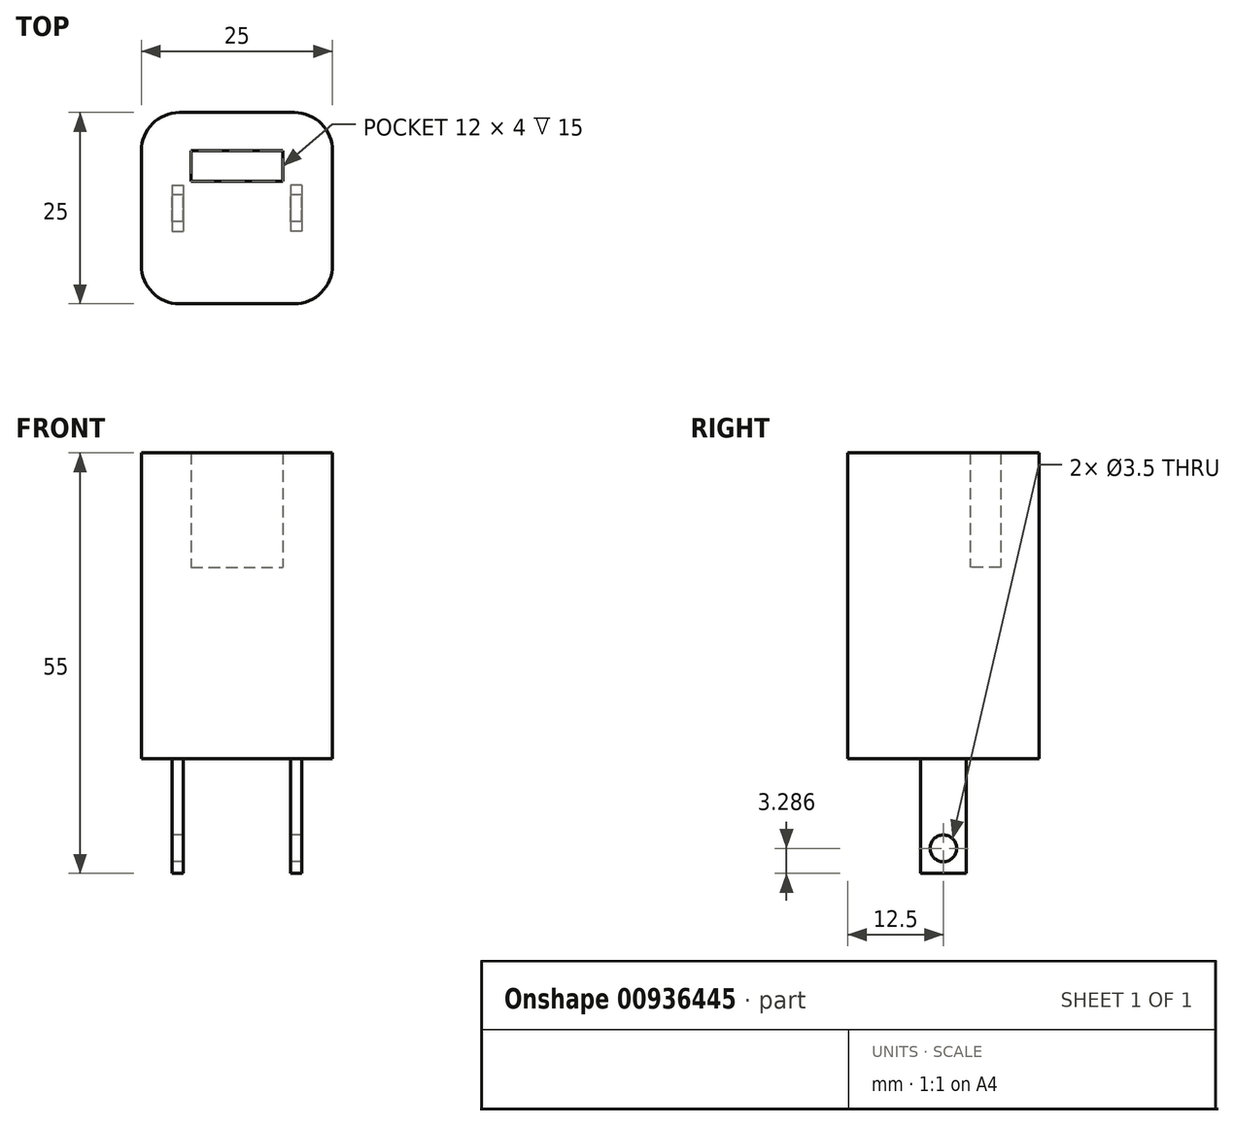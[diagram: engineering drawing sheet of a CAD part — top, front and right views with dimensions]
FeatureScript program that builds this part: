
annotation { "Feature Type Name" : "Feature", "Feature Type Description" : "" }
export const myFeature = defineFeature(function(context is Context, id is Id, definition is map)
    precondition{}
    {
        {
            var Q0;
            Q0=qCreatedBy(makeId("Top.planeOp"),FACE);
            var sketch = newSketch(context, id + "F0", { "sketchPlane" : qUnion([Q0])});
            skLineSegment(sketch, "E0.bottom", {"start": v(12.5, 12.5) * mm, "end": v(-12.5, 12.5) * mm});
            skLineSegment(sketch, "E0.top", {"start": v(12.5, -12.5) * mm, "end": v(-12.5, -12.5) * mm});
            skLineSegment(sketch, "E0.left", {"start": v(12.5, 12.5) * mm, "end": v(12.5, -12.5) * mm});
            skLineSegment(sketch, "E0.right", {"start": v(-12.5, 12.5) * mm, "end": v(-12.5, -12.5) * mm});
            skPoint(sketch, "E0.middle", {"position": v(0, 0) * mm});
            skLineSegment(sketch, "E1.bottom", {"start": v(-6, 7.5) * mm, "end": v(6, 7.5) * mm});
            skLineSegment(sketch, "E1.top", {"start": v(-6, 3.5) * mm, "end": v(6, 3.5) * mm});
            skLineSegment(sketch, "E1.left", {"start": v(-6, 7.5) * mm, "end": v(-6, 3.5) * mm});
            skLineSegment(sketch, "E1.right", {"start": v(6, 7.5) * mm, "end": v(6, 3.5) * mm});
            skSolve(sketch);
        }
        {
            var Q0;
            Q0=makeQuery(id+"F0.imprint","IMPRINT",FACE,{"disambiguationData":[TD([[makeQuery(id+"F0.imprint","IMPRINT",EDGE,{"derivedFrom":sQuery(id+"F0.wireOp",EDGE,"E0.bottom")}),1.0]])]});
            extrude(context, id + "F1", {"entities" : qUnion([Q0]), "depth" : 40 * mm, "offsetDistance" : 25 * mm});
        }
        {
            var Q0;
            Q0=makeQuery(id+"F1.opExtrude","CAP_FACE",FACE,{"disambiguationData":[OSD([sQuery(id+"F0.wireOp",EDGE,"E0.bottom"),sQuery(id+"F0.wireOp",EDGE,"E0.top"),sQuery(id+"F0.wireOp",EDGE,"E0.left"),sQuery(id+"F0.wireOp",EDGE,"E0.right"),sQuery(id+"F0.wireOp",EDGE,"E1.bottom"),sQuery(id+"F0.wireOp",EDGE,"E1.top"),sQuery(id+"F0.wireOp",EDGE,"E1.left"),sQuery(id+"F0.wireOp",EDGE,"E1.right")])],"isStart":true});
            var sketch = newSketch(context, id + "F2", { "sketchPlane" : qUnion([Q0])});
            skLineSegment(sketch, "E2.bottom", {"start": v(-8.5, -3) * mm, "end": v(-7, -3) * mm});
            skLineSegment(sketch, "E2.top", {"start": v(-8.5, 3) * mm, "end": v(-7, 3) * mm});
            skLineSegment(sketch, "E2.left", {"start": v(-8.5, -3) * mm, "end": v(-8.5, 3) * mm});
            skLineSegment(sketch, "E2.right", {"start": v(-7, -3) * mm, "end": v(-7, 3) * mm});
            skLineSegment(sketch, "E3.bottom", {"start": v(8.5, -3) * mm, "end": v(7, -3) * mm});
            skLineSegment(sketch, "E3.top", {"start": v(8.5, 3) * mm, "end": v(7, 3) * mm});
            skLineSegment(sketch, "E3.left", {"start": v(8.5, -3) * mm, "end": v(8.5, 3) * mm});
            skLineSegment(sketch, "E3.right", {"start": v(7, -3) * mm, "end": v(7, 3) * mm});
            skSolve(sketch);
        }
        {
            var Q0;
            Q0 = qSketchRegion(id + "F2", true);
            extrude(context, id + "F3", {"entities" : qUnion([Q0]), "operationType" : NewBodyOperationType.ADD, "depth" : 15 * mm, "offsetDistance" : 25 * mm});
        }
        {
            var Q0;
            Q0=makeQuery(id+"F3.opExtrude","SWEPT_FACE",FACE,{"disambiguationData":[OSD([sQuery(id+"F2.wireOp",EDGE,"E2.left")])]});
            var sketch = newSketch(context, id + "F4", { "sketchPlane" : qUnion([Q0])});
            skCircle(sketch, "E4", {"center": v(0, -11.71) * mm, "radius": 1.75 * mm});
            skSolve(sketch);
        }
        {
            var Q0;
            Q0 = qSketchRegion(id + "F4", true);
            extrude(context, id + "F5", {"entities" : qUnion([Q0]), "operationType" : NewBodyOperationType.REMOVE, "oppositeDirection" : true, "depth" : 25 * mm, "offsetDistance" : 25 * mm});
        }
        {
            var Q0;
            Q0=makeQuery(id+"F1.opExtrude","CAP_FACE",FACE,{"disambiguationData":[OSD([sQuery(id+"F0.wireOp",EDGE,"E0.bottom"),sQuery(id+"F0.wireOp",EDGE,"E0.top"),sQuery(id+"F0.wireOp",EDGE,"E0.left"),sQuery(id+"F0.wireOp",EDGE,"E0.right"),sQuery(id+"F0.wireOp",EDGE,"E1.bottom"),sQuery(id+"F0.wireOp",EDGE,"E1.top"),sQuery(id+"F0.wireOp",EDGE,"E1.left"),sQuery(id+"F0.wireOp",EDGE,"E1.right")])],"isStart":true});
            var sketch = newSketch(context, id + "F6", { "sketchPlane" : qUnion([Q0])});
            skLineSegment(sketch, "E5.bottom", {"start": v(6, -7.5) * mm, "end": v(-6, -7.5) * mm});
            skLineSegment(sketch, "E5.top", {"start": v(6, -3.5) * mm, "end": v(-6, -3.5) * mm});
            skLineSegment(sketch, "E5.left", {"start": v(6, -7.5) * mm, "end": v(6, -3.5) * mm});
            skLineSegment(sketch, "E5.right", {"start": v(-6, -7.5) * mm, "end": v(-6, -3.5) * mm});
            skSolve(sketch);
        }
        {
            var Q0;
            Q0 = qSketchRegion(id + "F6", true);
            extrude(context, id + "F7", {"entities" : qUnion([Q0]), "operationType" : NewBodyOperationType.ADD, "oppositeDirection" : true, "depth" : 25 * mm, "offsetDistance" : 25 * mm});
        }
        {
            var Q0;
            Q0=makeQuery(id+"F1.opExtrude","SWEPT_EDGE",EDGE,{"disambiguationData":[OSD([sQuery(id+"F0.wireOp",EDGE,"E0.bottom"),sQuery(id+"F0.wireOp",EDGE,"E0.left")])]});
            var Q1;
            Q1=makeQuery(id+"F1.opExtrude","SWEPT_EDGE",EDGE,{"disambiguationData":[OSD([sQuery(id+"F0.wireOp",EDGE,"E0.bottom"),sQuery(id+"F0.wireOp",EDGE,"E0.right")])]});
            var Q2;
            Q2=makeQuery(id+"F1.opExtrude","SWEPT_EDGE",EDGE,{"disambiguationData":[OSD([sQuery(id+"F0.wireOp",EDGE,"E0.top"),sQuery(id+"F0.wireOp",EDGE,"E0.left")])]});
            var Q3;
            Q3=makeQuery(id+"F1.opExtrude","SWEPT_EDGE",EDGE,{"disambiguationData":[OSD([sQuery(id+"F0.wireOp",EDGE,"E0.top"),sQuery(id+"F0.wireOp",EDGE,"E0.right")])]});
            fillet(context, id + "F8", {"entities" : qUnion([Q0, Q1, Q2, Q3]), "radius" : 5 * mm, "tangentPropagation" : true, "allowEdgeOverflow" : false});
        }
    });
